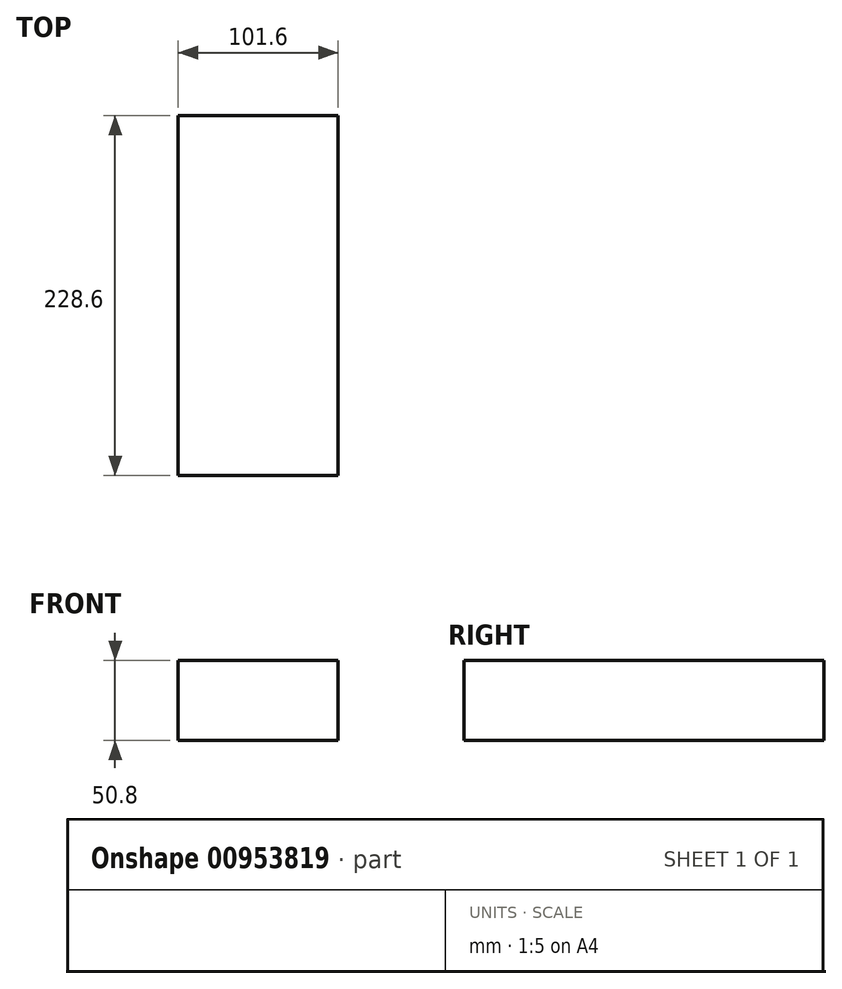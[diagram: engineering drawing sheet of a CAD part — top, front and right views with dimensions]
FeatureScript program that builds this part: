
annotation { "Feature Type Name" : "Feature", "Feature Type Description" : "" }
export const myFeature = defineFeature(function(context is Context, id is Id, definition is map)
    precondition{}
    {
        {
            var Q0;
            Q0=qCreatedBy(makeId("Front.planeOp"),FACE);
            var sketch = newSketch(context, id + "F0", { "sketchPlane" : qUnion([Q0])});
            skLineSegment(sketch, "E0.bottom", {"start": v(-50.8, -25.4) * mm, "end": v(50.8, -25.4) * mm});
            skLineSegment(sketch, "E0.top", {"start": v(-50.8, 25.4) * mm, "end": v(50.8, 25.4) * mm});
            skLineSegment(sketch, "E0.left", {"start": v(-50.8, -25.4) * mm, "end": v(-50.8, 25.4) * mm});
            skLineSegment(sketch, "E0.right", {"start": v(50.8, -25.4) * mm, "end": v(50.8, 25.4) * mm});
            skPoint(sketch, "E0.middle", {"position": v(0, 0) * mm});
            skSolve(sketch);
        }
        {
            var Q0;
            Q0 = qSketchRegion(id + "F0", true);
            extrude(context, id + "F1", {"entities" : qUnion([Q0]), "depth" : 228.6 * mm, "offsetDistance" : 25.4 * mm});
        }
    });
